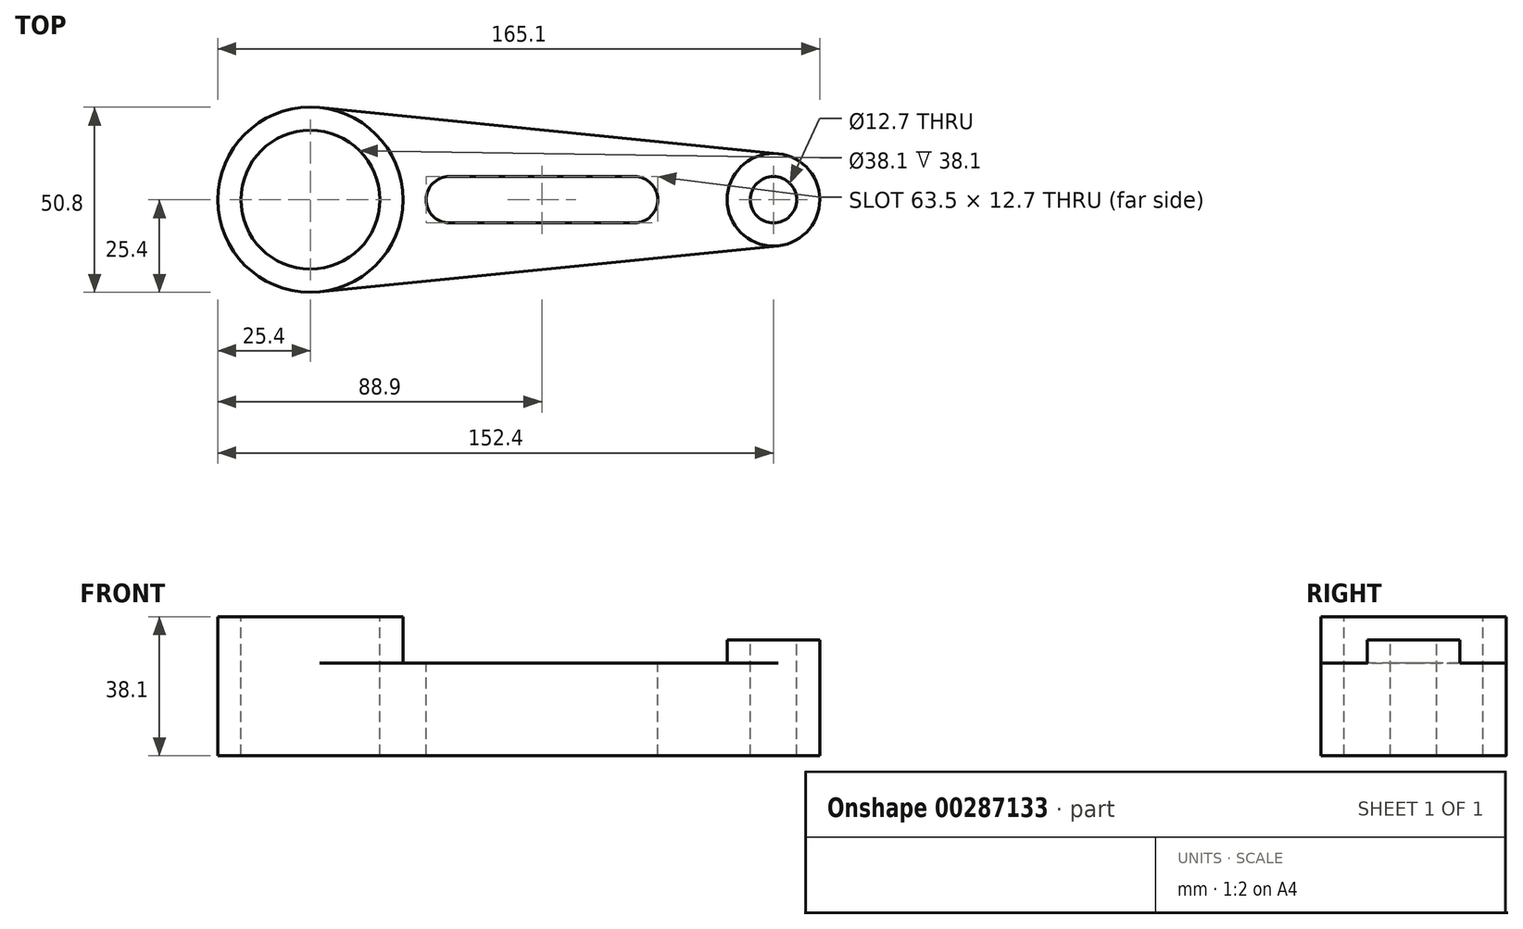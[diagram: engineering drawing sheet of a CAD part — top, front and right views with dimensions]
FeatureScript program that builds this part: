
annotation { "Feature Type Name" : "Feature", "Feature Type Description" : "" }
export const myFeature = defineFeature(function(context is Context, id is Id, definition is map)
    precondition{}
    {
        {
            var Q0;
            Q0=qCreatedBy(makeId("Top.planeOp"),FACE);
            var sketch = newSketch(context, id + "F0", { "sketchPlane" : qUnion([Q0])});
            skArc(sketch, "E0", {"start": v(0, 6.35) * mm, "mid": v(-6.35, 0) * mm, "end": v(0, -6.35) * mm});
            skCircle(sketch, "E1", {"center": v(-38.1, 0) * mm, "radius": 19.05 * mm});
            skCircle(sketch, "E2", {"center": v(-38.1, 0) * mm, "radius": 25.4 * mm});
            skArc(sketch, "E3", {"start": v(50.8, -6.35) * mm, "mid": v(57.15, 0) * mm, "end": v(50.8, 6.35) * mm});
            skCircle(sketch, "E4", {"center": v(88.9, 0) * mm, "radius": 12.7 * mm});
            skCircle(sketch, "E5", {"center": v(88.9, 0) * mm, "radius": 6.35 * mm});
            skLineSegment(sketch, "E6", {"start": v(0, 6.35) * mm, "end": v(50.8, 6.35) * mm});
            skLineSegment(sketch, "E7", {"start": v(0, -6.35) * mm, "end": v(50.8, -6.35) * mm});
            skLineSegment(sketch, "E8", {"start": v(-35.56, 25.27) * mm, "end": v(90.17, 12.64) * mm});
            skLineSegment(sketch, "E9", {"start": v(-35.56, -25.27) * mm, "end": v(90.17, -12.64) * mm});
            skSolve(sketch);
        }
        {
            var Q0;
            Q0=makeQuery(id+"F0.imprint","IMPRINT",FACE,{"disambiguationData":[TD([[makeQuery(id+"F0.imprint","IMPRINT",EDGE,{"derivedFrom":sQuery(id+"F0.wireOp",EDGE,"E1")}),-1.0]])]});
            var Q1;
            Q1=makeQuery(id+"F0.imprint","IMPRINT",FACE,{"disambiguationData":[TD([[makeQuery(id+"F0.imprint","IMPRINT",EDGE,{"derivedFrom":sQuery(id+"F0.wireOp",EDGE,"E0")}),-1.0]])]});
            var Q2;
            Q2=makeQuery(id+"F0.imprint","IMPRINT",FACE,{"disambiguationData":[TD([[makeQuery(id+"F0.imprint","IMPRINT",EDGE,{"derivedFrom":sQuery(id+"F0.wireOp",EDGE,"E5")}),-1.0]])]});
            extrude(context, id + "F1", {"entities" : qUnion([Q0, Q1, Q2]), "oppositeDirection" : true, "depth" : 38.1 * mm});
        }
        {
            var Q0;
            Q0=makeQuery(id+"F0.imprint","IMPRINT",FACE,{"disambiguationData":[TD([[makeQuery(id+"F0.imprint","IMPRINT",EDGE,{"derivedFrom":sQuery(id+"F0.wireOp",EDGE,"E5")}),-1.0]])]});
            extrude(context, id + "F2", {"entities" : qUnion([Q0]), "operationType" : NewBodyOperationType.REMOVE, "oppositeDirection" : true, "depth" : 6.35 * mm});
        }
        {
            var Q0;
            Q0=makeQuery(id+"F0.imprint","IMPRINT",FACE,{"disambiguationData":[TD([[makeQuery(id+"F0.imprint","IMPRINT",EDGE,{"derivedFrom":sQuery(id+"F0.wireOp",EDGE,"E0")}),-1.0]])]});
            extrude(context, id + "F3", {"entities" : qUnion([Q0]), "operationType" : NewBodyOperationType.REMOVE, "oppositeDirection" : true, "depth" : 12.7 * mm});
        }
    });
